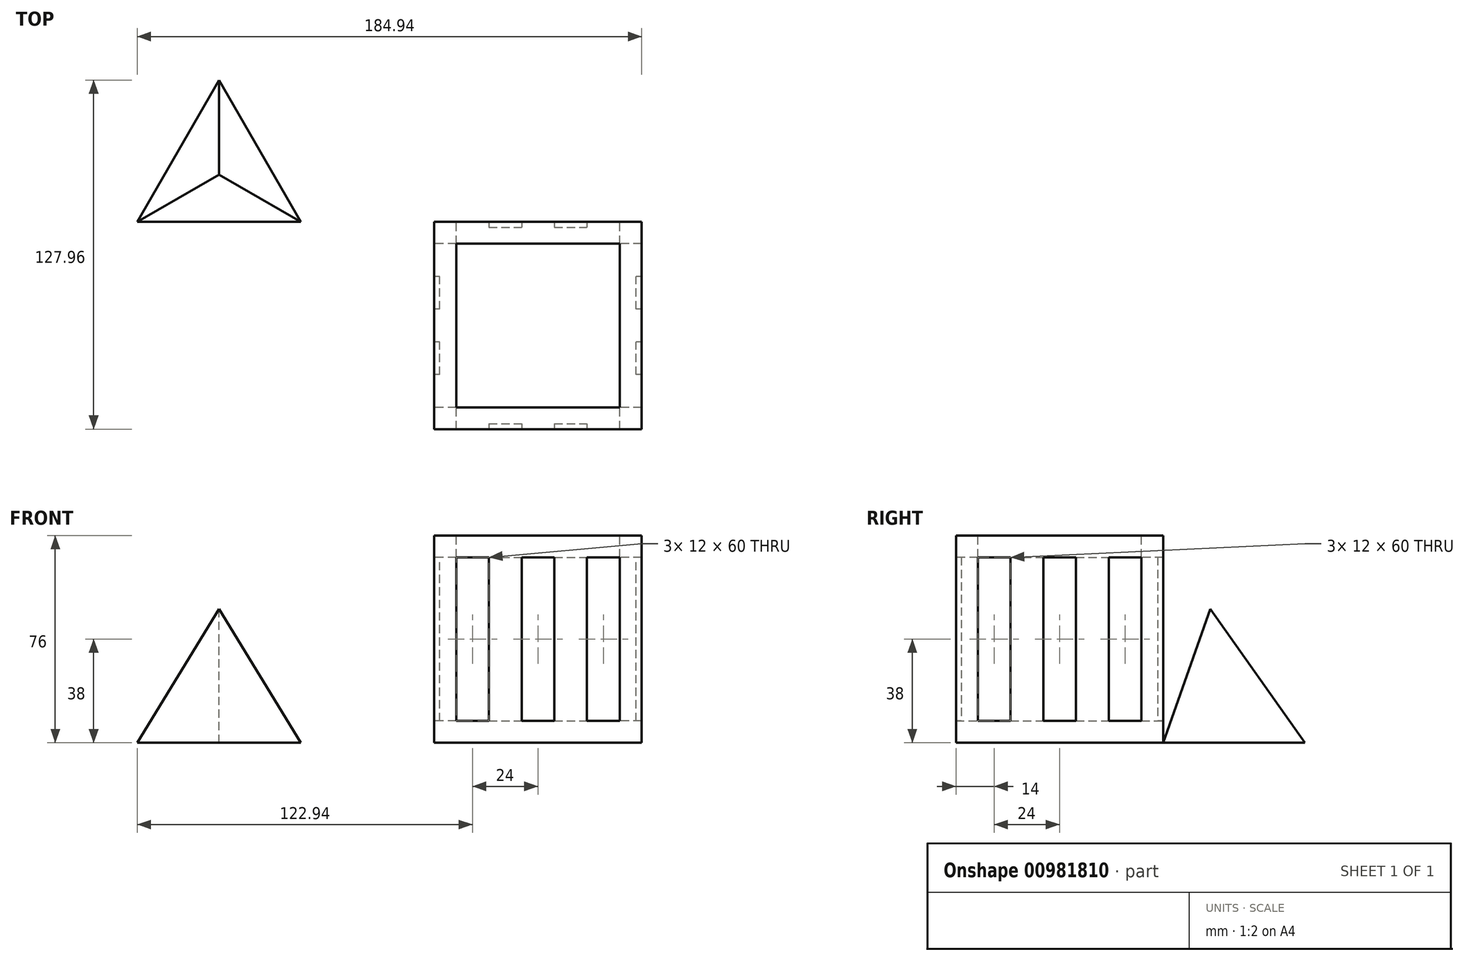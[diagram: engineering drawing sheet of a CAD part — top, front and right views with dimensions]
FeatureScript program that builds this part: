
annotation { "Feature Type Name" : "Feature", "Feature Type Description" : "" }
export const myFeature = defineFeature(function(context is Context, id is Id, definition is map)
    precondition{}
    {
        {
            var Q0;
            Q0=qCreatedBy(makeId("Right.planeOp"),FACE);
            var sketch = newSketch(context, id + "F0", { "sketchPlane" : qUnion([Q0])});
            skLineSegment(sketch, "E0.bottom", {"start": v(-76, 76) * mm, "end": v(0, 76) * mm});
            skLineSegment(sketch, "E0.top", {"start": v(-76, 0) * mm, "end": v(0, 0) * mm});
            skLineSegment(sketch, "E0.left", {"start": v(-76, 76) * mm, "end": v(-76, 0) * mm});
            skLineSegment(sketch, "E0.right", {"start": v(0, 76) * mm, "end": v(0, 0) * mm});
            skSolve(sketch);
        }
        {
            var Q0;
            Q0=makeQuery(id+"F0.imprint","IMPRINT",FACE,{"disambiguationData":[TD([[makeQuery(id+"F0.imprint","IMPRINT",EDGE,{"derivedFrom":sQuery(id+"F0.wireOp",EDGE,"E0.bottom")}),-1.0]])]});
            var Q1;
            Q1 = qSketchRegion(id + "F4", true);
            extrude(context, id + "F1", {"entities" : qUnion([Q0, Q1]), "depth" : 76 * mm, "offsetDistance" : 25 * mm});
        }
        {
            var Q0;
            Q0=makeQuery(id+"F1.opExtrude","SWEPT_FACE",FACE,{"disambiguationData":[OSD([sQuery(id+"F0.wireOp",EDGE,"E0.bottom")])]});
            var sketch = newSketch(context, id + "F2", { "sketchPlane" : qUnion([Q0])});
            skLineSegment(sketch, "E1.bottom", {"start": v(8, -68) * mm, "end": v(68, -68) * mm});
            skLineSegment(sketch, "E1.top", {"start": v(8, -8) * mm, "end": v(68, -8) * mm});
            skLineSegment(sketch, "E1.left", {"start": v(8, -68) * mm, "end": v(8, -8) * mm});
            skLineSegment(sketch, "E1.right", {"start": v(68, -68) * mm, "end": v(68, -8) * mm});
            skSolve(sketch);
        }
        {
            var Q0;
            Q0=makeQuery(id+"F2.imprint","IMPRINT",FACE,{"disambiguationData":[TD([[makeQuery(id+"F2.imprint","IMPRINT",EDGE,{"derivedFrom":sQuery(id+"F2.wireOp",EDGE,"E1.bottom")}),1.0]])]});
            extrude(context, id + "F3", {"entities" : qUnion([Q0]), "operationType" : NewBodyOperationType.REMOVE, "oppositeDirection" : true, "depth" : 68 * mm, "offsetDistance" : 25 * mm});
        }
        {
            var Q0;
            Q0=makeQuery(id+"F1.opExtrude","SWEPT_FACE",FACE,{"disambiguationData":[OSD([sQuery(id+"F0.wireOp",EDGE,"E0.left")])]});
            var sketch = newSketch(context, id + "F4", { "sketchPlane" : qUnion([Q0])});
            skLineSegment(sketch, "E2.bottom", {"start": v(8, 68) * mm, "end": v(68, 68) * mm});
            skLineSegment(sketch, "E2.top", {"start": v(8, 8) * mm, "end": v(68, 8) * mm});
            skLineSegment(sketch, "E2.left", {"start": v(8, 68) * mm, "end": v(8, 8) * mm});
            skLineSegment(sketch, "E2.right", {"start": v(68, 68) * mm, "end": v(68, 8) * mm});
            skLineSegment(sketch, "E3", {"start": v(20, 68) * mm, "end": v(20, 8) * mm});
            skLineSegment(sketch, "E4", {"start": v(32, 68) * mm, "end": v(32, 8) * mm});
            skLineSegment(sketch, "E5", {"start": v(44, 68) * mm, "end": v(44, 8) * mm});
            skLineSegment(sketch, "E6", {"start": v(56, 68) * mm, "end": v(56, 8) * mm});
            skSolve(sketch);
        }
        {
            var Q0;
            {var subQ0=sQuery(id+"F4.wireOp",EDGE,"E2.left");Q0=makeQuery(id+"F4.imprint","IMPRINT",FACE,{"disambiguationData":[TD([[makeQuery(id+"F4.imprint","IMPRINT",EDGE,{"derivedFrom":subQ0}),1.0]])]});}
            var Q1;
            {var subQ0=sQuery(id+"F4.wireOp",EDGE,"E4");Q1=makeQuery(id+"F4.imprint","IMPRINT",FACE,{"disambiguationData":[TD([[makeQuery(id+"F4.imprint","IMPRINT",EDGE,{"derivedFrom":subQ0}),1.0]])]});}
            var Q2;
            {var subQ0=sQuery(id+"F4.wireOp",EDGE,"E2.right");Q2=makeQuery(id+"F4.imprint","IMPRINT",FACE,{"disambiguationData":[TD([[makeQuery(id+"F4.imprint","IMPRINT",EDGE,{"derivedFrom":subQ0}),-1.0]])]});}
            extrude(context, id + "F5", {"entities" : qUnion([Q0, Q1, Q2]), "operationType" : NewBodyOperationType.REMOVE, "oppositeDirection" : true, "depth" : 100 * mm, "offsetDistance" : 25 * mm});
        }
        {
            var Q0;
            Q0=makeQuery(id+"F3.boolean.opBoolean","COPY",FACE,{"derivedFrom":makeQuery(id+"F3.opExtrude","SWEPT_FACE",FACE,{"disambiguationData":[OSD([sQuery(id+"F2.wireOp",EDGE,"E1.bottom")])]})});
            var sketch = newSketch(context, id + "F6", { "sketchPlane" : qUnion([Q0])});
            skLineSegment(sketch, "E7", {"start": v(-56, 68) * mm, "end": v(-44, 68) * mm});
            skLineSegment(sketch, "E8", {"start": v(-32, 68) * mm, "end": v(-20, 68) * mm});
            skSolve(sketch);
        }
        {
            var Q0;
            Q0=makeQuery(id+"F6.imprint","IMPRINT",FACE,{"disambiguationData":[TD([[makeQuery(id+"F6.imprint","IMPRINT",EDGE,{"derivedFrom":sQuery(id+"F6.wireOp",EDGE,"E7")}),-1.0]])]});
            var Q1;
            Q1=makeQuery(id+"F6.imprint","IMPRINT",FACE,{"disambiguationData":[TD([[makeQuery(id+"F6.imprint","IMPRINT",EDGE,{"derivedFrom":sQuery(id+"F6.wireOp",EDGE,"E8")}),-1.0]])]});
            extrude(context, id + "F7", {"entities" : qUnion([Q0, Q1]), "operationType" : NewBodyOperationType.REMOVE, "oppositeDirection" : true, "depth" : 6 * mm, "offsetDistance" : 25 * mm});
        }
        {
            var Q0;
            Q0=makeQuery(id+"F3.boolean.opBoolean","COPY",FACE,{"derivedFrom":makeQuery(id+"F3.opExtrude","SWEPT_FACE",FACE,{"disambiguationData":[OSD([sQuery(id+"F2.wireOp",EDGE,"E1.top")])]})});
            var sketch = newSketch(context, id + "F8", { "sketchPlane" : qUnion([Q0])});
            skLineSegment(sketch, "E9", {"start": v(20, 68) * mm, "end": v(32, 68) * mm});
            skLineSegment(sketch, "E10", {"start": v(44, 68) * mm, "end": v(56, 68) * mm});
            skSolve(sketch);
        }
        {
            var Q0;
            Q0=makeQuery(id+"F8.imprint","IMPRINT",FACE,{"disambiguationData":[TD([[makeQuery(id+"F8.imprint","IMPRINT",EDGE,{"derivedFrom":sQuery(id+"F8.wireOp",EDGE,"E10")}),-1.0]])]});
            var Q1;
            Q1=makeQuery(id+"F8.imprint","IMPRINT",FACE,{"disambiguationData":[TD([[makeQuery(id+"F8.imprint","IMPRINT",EDGE,{"derivedFrom":sQuery(id+"F8.wireOp",EDGE,"E9")}),-1.0]])]});
            extrude(context, id + "F9", {"entities" : qUnion([Q0, Q1]), "operationType" : NewBodyOperationType.REMOVE, "oppositeDirection" : true, "depth" : 6 * mm, "offsetDistance" : 25 * mm});
        }
        {
            var Q0;
            Q0=makeQuery(id+"F1.opExtrude","CAP_FACE",FACE,{"disambiguationData":[OSD([sQuery(id+"F0.wireOp",EDGE,"E0.bottom"),sQuery(id+"F0.wireOp",EDGE,"E0.top"),sQuery(id+"F0.wireOp",EDGE,"E0.left"),sQuery(id+"F0.wireOp",EDGE,"E0.right")])],"isStart":true});
            var sketch = newSketch(context, id + "F10", { "sketchPlane" : qUnion([Q0])});
            skLineSegment(sketch, "E11.bottom", {"start": v(8, 68) * mm, "end": v(68, 68) * mm});
            skLineSegment(sketch, "E11.top", {"start": v(8, 8) * mm, "end": v(68, 8) * mm});
            skLineSegment(sketch, "E11.left", {"start": v(8, 68) * mm, "end": v(8, 8) * mm});
            skLineSegment(sketch, "E11.right", {"start": v(68, 68) * mm, "end": v(68, 8) * mm});
            skLineSegment(sketch, "E12", {"start": v(20, 68) * mm, "end": v(20, 8) * mm});
            skLineSegment(sketch, "E13", {"start": v(32, 68) * mm, "end": v(32, 8) * mm});
            skLineSegment(sketch, "E14", {"start": v(44, 68) * mm, "end": v(44, 8) * mm});
            skLineSegment(sketch, "E15", {"start": v(56, 68) * mm, "end": v(56, 8) * mm});
            skSolve(sketch);
        }
        {
            var Q0;
            {var subQ0=sQuery(id+"F10.wireOp",EDGE,"E11.left");Q0=makeQuery(id+"F10.imprint","IMPRINT",FACE,{"disambiguationData":[TD([[makeQuery(id+"F10.imprint","IMPRINT",EDGE,{"derivedFrom":subQ0}),1.0]])]});}
            var Q1;
            {var subQ0=sQuery(id+"F10.wireOp",EDGE,"E13");Q1=makeQuery(id+"F10.imprint","IMPRINT",FACE,{"disambiguationData":[TD([[makeQuery(id+"F10.imprint","IMPRINT",EDGE,{"derivedFrom":subQ0}),1.0]])]});}
            var Q2;
            {var subQ0=sQuery(id+"F10.wireOp",EDGE,"E11.right");Q2=makeQuery(id+"F10.imprint","IMPRINT",FACE,{"disambiguationData":[TD([[makeQuery(id+"F10.imprint","IMPRINT",EDGE,{"derivedFrom":subQ0}),-1.0]])]});}
            extrude(context, id + "F11", {"entities" : qUnion([Q0, Q1, Q2]), "operationType" : NewBodyOperationType.REMOVE, "oppositeDirection" : true, "depth" : 99 * mm, "offsetDistance" : 25 * mm});
        }
        {
            var Q0;
            {var subQ11=sQuery(id+"F4.wireOp",EDGE,"E2.left");var subQ12=makeQuery(id+"F5.opExtrude","SWEPT_FACE",FACE,{"disambiguationData":[OSD([subQ11])]});var subQ15=sQuery(id+"F2.wireOp",EDGE,"E1.left");var subQ16=makeQuery(id+"F3.boolean.opBoolean","COPY",FACE,{"derivedFrom":makeQuery(id+"F3.opExtrude","SWEPT_FACE",FACE,{"disambiguationData":[OSD([subQ15])]})});Q0=makeQuery(id+"F11.boolean.opBoolean","SPLIT",FACE,{"disambiguationData":[TD([makeQuery(id+"F1.opExtrude","SWEPT_FACE",FACE,{"disambiguationData":[OSD([sQuery(id+"F0.wireOp",EDGE,"E0.bottom")])]})])],"derivedFrom":makeQuery(id+"F5.boolean.opBoolean","MERGE",FACE,{"derivedFrom":[subQ16],"fromTools":[subQ12]})});}
            var sketch = newSketch(context, id + "F12", { "sketchPlane" : qUnion([Q0])});
            skLineSegment(sketch, "E16", {"start": v(-56, 68) * mm, "end": v(-44, 68) * mm});
            skLineSegment(sketch, "E17", {"start": v(-32, 68) * mm, "end": v(-20, 68) * mm});
            skSolve(sketch);
        }
        {
            var Q0;
            Q0=makeQuery(id+"F12.imprint","IMPRINT",FACE,{"disambiguationData":[TD([[makeQuery(id+"F12.imprint","IMPRINT",EDGE,{"derivedFrom":sQuery(id+"F12.wireOp",EDGE,"E17")}),-1.0]])]});
            var Q1;
            Q1=makeQuery(id+"F12.imprint","IMPRINT",FACE,{"disambiguationData":[TD([[makeQuery(id+"F12.imprint","IMPRINT",EDGE,{"derivedFrom":sQuery(id+"F12.wireOp",EDGE,"E16")}),-1.0]])]});
            extrude(context, id + "F13", {"entities" : qUnion([Q0, Q1]), "operationType" : NewBodyOperationType.REMOVE, "oppositeDirection" : true, "depth" : 6 * mm, "offsetDistance" : 25 * mm});
        }
        {
            var Q0;
            {var subQ27=sQuery(id+"F2.wireOp",EDGE,"E1.right");var subQ28=makeQuery(id+"F3.boolean.opBoolean","COPY",FACE,{"derivedFrom":makeQuery(id+"F3.opExtrude","SWEPT_FACE",FACE,{"disambiguationData":[OSD([subQ27])]})});var subQ29=sQuery(id+"F4.wireOp",EDGE,"E2.right");var subQ30=makeQuery(id+"F5.opExtrude","SWEPT_FACE",FACE,{"disambiguationData":[OSD([subQ29])]});Q0=makeQuery(id+"F11.boolean.opBoolean","SPLIT",FACE,{"disambiguationData":[TD([makeQuery(id+"F1.opExtrude","SWEPT_FACE",FACE,{"disambiguationData":[OSD([sQuery(id+"F0.wireOp",EDGE,"E0.bottom")])]})])],"derivedFrom":makeQuery(id+"F5.boolean.opBoolean","MERGE",FACE,{"derivedFrom":[subQ28],"fromTools":[subQ30]})});}
            var sketch = newSketch(context, id + "F14", { "sketchPlane" : qUnion([Q0])});
            skLineSegment(sketch, "E18", {"start": v(56, 68) * mm, "end": v(44, 68) * mm});
            skLineSegment(sketch, "E19", {"start": v(32, 68) * mm, "end": v(20, 68) * mm});
            skSolve(sketch);
        }
        {
            var Q0;
            Q0=makeQuery(id+"F14.imprint","IMPRINT",FACE,{"disambiguationData":[TD([[makeQuery(id+"F14.imprint","IMPRINT",EDGE,{"derivedFrom":sQuery(id+"F14.wireOp",EDGE,"E18")}),1.0]])]});
            var Q1;
            Q1=makeQuery(id+"F14.imprint","IMPRINT",FACE,{"disambiguationData":[TD([[makeQuery(id+"F14.imprint","IMPRINT",EDGE,{"derivedFrom":sQuery(id+"F14.wireOp",EDGE,"E19")}),1.0]])]});
            extrude(context, id + "F15", {"entities" : qUnion([Q0, Q1]), "operationType" : NewBodyOperationType.REMOVE, "oppositeDirection" : true, "depth" : 6 * mm, "offsetDistance" : 25 * mm});
        }
        {
            var Q0;
            Q0=qCreatedBy(makeId("Top.planeOp"),FACE);
            var sketch = newSketch(context, id + "F16", { "sketchPlane" : qUnion([Q0])});
            skLineSegment(sketch, "E20", {"start": v(-108.94, 0) * mm, "end": v(-78.94, 51.96) * mm});
            skLineSegment(sketch, "E21", {"start": v(-48.94, 0) * mm, "end": v(-108.94, 0) * mm});
            skLineSegment(sketch, "E22", {"start": v(-78.94, 51.96) * mm, "end": v(-48.94, 0) * mm});
            skPoint(sketch, "E23.orphan", {"position": v(11.06, 0) * mm});
            skPoint(sketch, "E24", {"position": v(-48.94, 0) * mm});
            skPoint(sketch, "E25", {"position": v(-93.94, 25.98) * mm});
            skLineSegment(sketch, "E26", {"start": v(-48.94, 0) * mm, "end": v(-93.94, 25.98) * mm});
            skLineSegment(sketch, "E27", {"start": v(-78.94, 51.96) * mm, "end": v(-78.94, 0) * mm});
            skLineSegment(sketch, "E28", {"start": v(-108.94, 0) * mm, "end": v(-63.94, 25.98) * mm});
            skPoint(sketch, "E29", {"position": v(-78.94, 17.32) * mm});
            skSolve(sketch);
        }
        {
            var Q0;
            {var subQ1=sQuery(id+"F16.wireOp",EDGE,"E22");var subQ3=sQuery(id+"F16.wireOp",EDGE,"E28");var subQ4=makeQuery(id+"F16.imprint","INTERSECT",VERTEX,{"derivedFrom":[subQ1,subQ3]});Q0=makeQuery(id+"F16.imprint","IMPRINT",FACE,{"disambiguationData":[TD([[makeQuery(id+"F16.imprint","IMPRINT",EDGE,{"disambiguationData":[TD([[subQ4,-1.0]])],"derivedFrom":subQ1}),-1.0]])]});}
            var Q1;
            {var subQ1=sQuery(id+"F16.wireOp",EDGE,"E22");var subQ3=sQuery(id+"F16.wireOp",EDGE,"E28");var subQ4=makeQuery(id+"F16.imprint","INTERSECT",VERTEX,{"derivedFrom":[subQ1,subQ3]});Q1=makeQuery(id+"F16.imprint","IMPRINT",FACE,{"disambiguationData":[TD([[makeQuery(id+"F16.imprint","IMPRINT",EDGE,{"disambiguationData":[TD([[subQ4,1.0]])],"derivedFrom":subQ1}),-1.0]])]});}
            var Q2;
            {var subQ1=sQuery(id+"F16.wireOp",EDGE,"E20");var subQ3=sQuery(id+"F16.wireOp",EDGE,"E26");var subQ4=makeQuery(id+"F16.imprint","INTERSECT",VERTEX,{"derivedFrom":[subQ1,subQ3]});Q2=makeQuery(id+"F16.imprint","IMPRINT",FACE,{"disambiguationData":[TD([[makeQuery(id+"F16.imprint","IMPRINT",EDGE,{"disambiguationData":[TD([[subQ4,-1.0]])],"derivedFrom":subQ1}),-1.0]])]});}
            var Q3;
            {var subQ1=sQuery(id+"F16.wireOp",EDGE,"E20");var subQ3=sQuery(id+"F16.wireOp",EDGE,"E26");var subQ4=makeQuery(id+"F16.imprint","INTERSECT",VERTEX,{"derivedFrom":[subQ1,subQ3]});Q3=makeQuery(id+"F16.imprint","IMPRINT",FACE,{"disambiguationData":[TD([[makeQuery(id+"F16.imprint","IMPRINT",EDGE,{"disambiguationData":[TD([[subQ4,1.0]])],"derivedFrom":subQ1}),-1.0]])]});}
            var Q4;
            {var subQ1=sQuery(id+"F16.wireOp",EDGE,"E21");var subQ3=sQuery(id+"F16.wireOp",EDGE,"E27");var subQ4=makeQuery(id+"F16.imprint","INTERSECT",VERTEX,{"derivedFrom":[subQ1,subQ3]});Q4=makeQuery(id+"F16.imprint","IMPRINT",FACE,{"disambiguationData":[TD([[makeQuery(id+"F16.imprint","IMPRINT",EDGE,{"disambiguationData":[TD([[subQ4,-1.0]])],"derivedFrom":subQ1}),-1.0]])]});}
            var Q5;
            {var subQ1=sQuery(id+"F16.wireOp",EDGE,"E21");var subQ3=sQuery(id+"F16.wireOp",EDGE,"E27");var subQ4=makeQuery(id+"F16.imprint","INTERSECT",VERTEX,{"derivedFrom":[subQ1,subQ3]});Q5=makeQuery(id+"F16.imprint","IMPRINT",FACE,{"disambiguationData":[TD([[makeQuery(id+"F16.imprint","IMPRINT",EDGE,{"disambiguationData":[TD([[subQ4,1.0]])],"derivedFrom":subQ1}),-1.0]])]});}
            extrude(context, id + "F17", {"entities" : qUnion([Q0, Q1, Q2, Q3, Q4, Q5]), "depth" : 49 * mm, "offsetDistance" : 25 * mm});
        }
        {
            var Q0;
            Q0=makeQuery(id+"F17.opExtrude","CAP_FACE",FACE,{"disambiguationData":[OSD([sQuery(id+"F16.wireOp",EDGE,"E20"),sQuery(id+"F16.wireOp",EDGE,"E21"),sQuery(id+"F16.wireOp",EDGE,"E22")])],"isStart":false});
            var sketch = newSketch(context, id + "F18", { "sketchPlane" : qUnion([Q0])});
            skLineSegment(sketch, "E30", {"start": v(-108.94, 0) * mm, "end": v(-78.94, 51.96) * mm});
            skLineSegment(sketch, "E31", {"start": v(-48.94, 0) * mm, "end": v(-108.94, 0) * mm});
            skLineSegment(sketch, "E32", {"start": v(-78.94, 51.96) * mm, "end": v(-48.94, 0) * mm});
            skPoint(sketch, "E33.orphan", {"position": v(11.06, 0) * mm});
            skPoint(sketch, "E34", {"position": v(-48.94, 0) * mm});
            skPoint(sketch, "E35", {"position": v(-93.94, 25.98) * mm});
            skLineSegment(sketch, "E36", {"start": v(-48.94, 0) * mm, "end": v(-93.94, 25.98) * mm});
            skLineSegment(sketch, "E37", {"start": v(-78.94, 51.96) * mm, "end": v(-78.94, 0) * mm});
            skLineSegment(sketch, "E38", {"start": v(-108.94, 0) * mm, "end": v(-63.94, 25.98) * mm});
            skPoint(sketch, "E39", {"position": v(-78.94, 17.32) * mm});
            skSolve(sketch);
        }
        {
            var Q0;
            Q0=sQuery(id+"F18.wireOp",VERTEX,"E39");
            var Q1;
            Q1=makeQuery(id+"F17.opExtrude","CAP_VERTEX",VERTEX,{"disambiguationData":[OSD([sQuery(id+"F16.wireOp",EDGE,"E20"),sQuery(id+"F16.wireOp",EDGE,"E22"),sQuery(id+"F16.wireOp",EDGE,"E27")])],"isStart":true});
            var Q2;
            Q2=makeQuery(id+"F17.opExtrude","CAP_VERTEX",VERTEX,{"disambiguationData":[OSD([sQuery(id+"F16.wireOp",EDGE,"E20"),sQuery(id+"F16.wireOp",EDGE,"E21"),sQuery(id+"F16.wireOp",EDGE,"E28")])],"isStart":true});
            cPlane(context, id + "F19", {"entities" : qUnion([Q0, Q1, Q2]), "cplaneType" : CPlaneType.THREE_POINT, "offset" : 25 * mm, "width" : 150 * mm, "height" : 150 * mm});
        }
        {
            var Q0;
            Q0=qCreatedBy(id+"F19.planeOp",FACE);
            var sketch = newSketch(context, id + "F20", { "sketchPlane" : qUnion([Q0])});
            skLineSegment(sketch, "E40.bottom", {"start": v(-77.53, 22.85) * mm, "end": v(19.08, 22.85) * mm});
            skLineSegment(sketch, "E40.top", {"start": v(-77.53, -46.2) * mm, "end": v(19.08, -46.2) * mm});
            skLineSegment(sketch, "E40.left", {"start": v(-77.53, 22.85) * mm, "end": v(-77.53, -46.2) * mm});
            skLineSegment(sketch, "E40.right", {"start": v(19.08, 22.85) * mm, "end": v(19.08, -46.2) * mm});
            skSolve(sketch);
        }
        {
            var Q0;
            Q0=makeQuery(id+"F20.imprint","IMPRINT",FACE,{"disambiguationData":[TD([[makeQuery(id+"F20.imprint","IMPRINT",EDGE,{"derivedFrom":sQuery(id+"F20.wireOp",EDGE,"E40.bottom")}),-1.0]])]});
            extrude(context, id + "F21", {"entities" : qUnion([Q0]), "operationType" : NewBodyOperationType.REMOVE, "oppositeDirection" : true, "depth" : 25 * mm, "offsetDistance" : 25 * mm});
        }
        {
            var Q0;
            Q0=sQuery(id+"F18.wireOp",VERTEX,"E39");
            var Q1;
            Q1=makeQuery(id+"F17.opExtrude","CAP_VERTEX",VERTEX,{"disambiguationData":[OSD([sQuery(id+"F16.wireOp",EDGE,"E20"),sQuery(id+"F16.wireOp",EDGE,"E22"),sQuery(id+"F16.wireOp",EDGE,"E27")])],"isStart":true});
            var Q2;
            Q2=makeQuery(id+"F17.opExtrude","CAP_VERTEX",VERTEX,{"disambiguationData":[OSD([sQuery(id+"F16.wireOp",EDGE,"E21"),sQuery(id+"F16.wireOp",EDGE,"E22"),sQuery(id+"F16.wireOp",EDGE,"E26")])],"isStart":true});
            cPlane(context, id + "F22", {"entities" : qUnion([Q0, Q1, Q2]), "cplaneType" : CPlaneType.THREE_POINT, "offset" : 25 * mm, "width" : 150 * mm, "height" : 150 * mm});
        }
        {
            var Q0;
            Q0=qCreatedBy(id+"F22.planeOp",FACE);
            var sketch = newSketch(context, id + "F23", { "sketchPlane" : qUnion([Q0])});
            skLineSegment(sketch, "E41.bottom", {"start": v(9.23, 77.71) * mm, "end": v(84.05, 77.71) * mm});
            skLineSegment(sketch, "E41.top", {"start": v(9.23, 4.73) * mm, "end": v(84.05, 4.73) * mm});
            skLineSegment(sketch, "E41.left", {"start": v(9.23, 77.71) * mm, "end": v(9.23, 4.73) * mm});
            skLineSegment(sketch, "E41.right", {"start": v(84.05, 77.71) * mm, "end": v(84.05, 4.73) * mm});
            skSolve(sketch);
        }
        {
            var Q0;
            Q0=makeQuery(id+"F23.imprint","IMPRINT",FACE,{"disambiguationData":[TD([[makeQuery(id+"F23.imprint","IMPRINT",EDGE,{"derivedFrom":sQuery(id+"F23.wireOp",EDGE,"E41.bottom")}),-1.0]])]});
            extrude(context, id + "F24", {"entities" : qUnion([Q0]), "operationType" : NewBodyOperationType.REMOVE, "depth" : 25 * mm, "offsetDistance" : 25 * mm});
        }
        {
            var Q0;
            Q0=sQuery(id+"F18.wireOp",VERTEX,"E39");
            var Q1;
            Q1=makeQuery(id+"F17.opExtrude","CAP_VERTEX",VERTEX,{"disambiguationData":[OSD([sQuery(id+"F16.wireOp",EDGE,"E20"),sQuery(id+"F16.wireOp",EDGE,"E21"),sQuery(id+"F16.wireOp",EDGE,"E28")])],"isStart":true});
            var Q2;
            Q2=makeQuery(id+"F17.opExtrude","CAP_VERTEX",VERTEX,{"disambiguationData":[OSD([sQuery(id+"F16.wireOp",EDGE,"E21"),sQuery(id+"F16.wireOp",EDGE,"E22"),sQuery(id+"F16.wireOp",EDGE,"E26")])],"isStart":true});
            cPlane(context, id + "F25", {"entities" : qUnion([Q0, Q1, Q2]), "cplaneType" : CPlaneType.THREE_POINT, "offset" : 25 * mm, "width" : 150 * mm, "height" : 150 * mm});
        }
        {
            var Q0;
            Q0=qCreatedBy(id+"F25.planeOp",FACE);
            var sketch = newSketch(context, id + "F26", { "sketchPlane" : qUnion([Q0])});
            skLineSegment(sketch, "E42.bottom", {"start": v(125.16, 80.24) * mm, "end": v(17.13, 80.24) * mm});
            skLineSegment(sketch, "E42.top", {"start": v(125.16, -31.93) * mm, "end": v(17.13, -31.93) * mm});
            skLineSegment(sketch, "E42.left", {"start": v(125.16, 80.24) * mm, "end": v(125.16, -31.93) * mm});
            skLineSegment(sketch, "E42.right", {"start": v(17.13, 80.24) * mm, "end": v(17.13, -31.93) * mm});
            skSolve(sketch);
        }
        {
            var Q0;
            Q0 = qSketchRegion(id + "F26", true);
            extrude(context, id + "F27", {"entities" : qUnion([Q0]), "operationType" : NewBodyOperationType.REMOVE, "oppositeDirection" : true, "depth" : 25 * mm, "offsetDistance" : 25 * mm});
        }
    });
